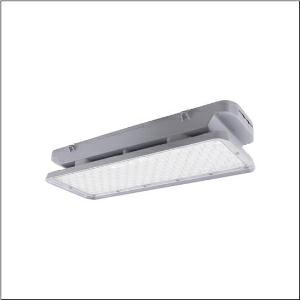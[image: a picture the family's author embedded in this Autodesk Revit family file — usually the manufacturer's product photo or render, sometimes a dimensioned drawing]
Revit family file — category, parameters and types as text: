
# Revit family: highbay_21-s_51hk41da4gca
name_source: partatom
category: Lighting Fixtures
units: mm (PartAtom-declared; Revit-internal decimal feet)

## family parameters
Cut with Voids When Loaded = No
Host = Face
Light Source = No
Part Type = Normal
Room Calculation Point = No
Round Connector Dimension = Use Diameter
Shared = No

## types (1)
- Highbay 21-S (1 x LED, 13400 lm, 75 W, 4000K)
    Apparent Load = 75 VA
    CIE Flux Codes = 87 97 99 100 100
    Color Rendering = 80
    Color Temperature = 4000K
    Default Elevation = 1800 mm
    Description = Highbay 21-S, LED high bay luminaire, primary light control with lens, of PC, light emission: direct distribution, primary light characteristic: symmetric, installation type: suspended mounting, surface-mounted, LED, rated luminous flux: 13.400lm, luminous efficacy: 180lm/W, light colour: 840, colour temperature: 4000K, with terminal, 5-pole, max. 2.5mm², mains connection: 220..240V, AC, 50Hz, rated input power: 75W, housing, of diecast aluminium, coated, grey, length: 471mm, width: 172mm, height: 87mm, protection rating (complete): IP66, insulation class (complete): insulation class I (protective earthing), certification: CE, ENEC, UKCA, protection symbol: D, impact resistance: IK08, permissible operating ambient temperature: -30..+60°C, corresponds to IFS (International Featured Standards) requirements for safety and quality in the food industry, LABS conformity tested according to VDMA 24364:2018-05, packaging unit: 1 piece
    Height = 89 mm
    Lamp = 1 x LED
    Lamp Light Flux = 13400 lm
    Lamp Power = 75 W
    Lamp count = 1
    Length = 471 mm
    Luminous efficacy = 179 lm/W
    Manufacturer = Siteco
    ModVariant = No
    Model = 51HK41DA4GCA
    Mounting Place = Ceiling
    Mounting Type = Pendant
    Number of Poles = 1
    OnlyDefault = Yes
    Power Factor = 1
    Product Name = Highbay 21-S
    Product group = LED high bay luminaire
    ProductGroupID = 903
    Protection Class = Protection class I
    Protection Degree = IP 66
    RLX_Detail_Level = 1
    RLX_Emergency_Light_Flux = 0 lm
    RLX_Emergency_Type = 0
    RLX_Emergency_Type_DB = No
    RlxData = <blob elided: 21437 chars, md5=87ee32b1>
    Socket = socket
    Standby Power = 0 W
    System Light Flux = 13400 lm
    System Power = 75 W
    Type Comments = Product without accessories
    Type Image = l_1276526.jpg
    URL = http://relux.com
    VarID = ---
    Voltage = 0 V
    Weight = 0.00 kg
    Width = 172 mm

## geometry (parser evidence)
native form markers: Blend x4, Sweep x12
no freeform markers — native parametric forms only
